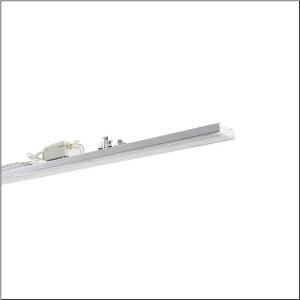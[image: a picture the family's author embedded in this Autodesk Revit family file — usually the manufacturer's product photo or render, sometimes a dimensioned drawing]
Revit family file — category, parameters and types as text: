
# Revit family: licross_r__21_recessed_mo_52te10dv4e5g_8208
name_source: partatom
category: Lighting Fixtures
units: mm (PartAtom-declared; Revit-internal decimal feet)

## family parameters
Cut with Voids When Loaded = No
Host = Face
Light Source = No
Part Type = Normal
Room Calculation Point = No
Round Connector Dimension = Use Diameter
Shared = No

## types (1)
- --- (1 x LED, 14990 lm, 85.3 W, 4000K)
    Apparent Load = 85 VA
    CIE Flux Codes = 50 81 96 100 100
    Color Rendering = 80
    Color Temperature = 4000K
    Default Elevation = 1800 mm
    Description = Licross® 21 Recessed MO, luminaire insert, of sheet steel, galvanised, coil coated, white, length: 2.250mm, width: 66mm, height: 67mm, LED rated luminous flux: 14.990lm, light colour: 840, control gear: DALI 2, with plug, 5-pole, with phase selection, mains connection: 220..240V, AC, 50/60Hz, rated input power: 85W, halogen-free wiring, primary optical cover: cover, of PMMA, light emission: direct distribution, primary light characteristic: symmetric, protection rating (complete): IP54, insulation class (complete): insulation class I (protective earthing), certification: CE, ENEC, VDE, UKCA, protection symbol: D if used in an environment with non-conductive dust loads with corresponding accessories, impact resistance: IK06, permissible ambient temperature for indoor applications: -25..+35°C, corresponds to IFS (International Featured Standards) requirements for safety and quality in the food industry, reducing of maximum allowable ambient temperature of 5°C with ceiling mounting, LABS conformity tested according to VDMA 24364:2018-05, packaging unit: 1 piece
    Height = 58 mm
    Lamp = 1 x LED
    Lamp Light Flux = 14990 lm
    Lamp Power = 85.3 W
    Lamp count = 1
    Length = 2250 mm
    Luminous efficacy = 176 lm/W
    Manufacturer = Siteco
    ModVariant = No
    Model = 52TE10DV4E5G
    Mounting Place = Ceiling
    Mounting Type = Pendant
    Number of Poles = 1
    OnlyDefault = Yes
    Power Factor = 1
    Product Name = Licross® 21 Recessed MO
    Product group = luminaire insert
    ProductGroupID = 901
    Protection Class = Protection class I
    Protection Degree = IP 54
    RLX_Detail_Level = 1
    RLX_Emergency_Light_Flux = 0 lm
    RLX_Emergency_Type = 0
    RLX_Emergency_Type_DB = No
    RlxData = <blob elided: 29341 chars, md5=07ba838a>
    Socket = socket
    Standby Power = 0 W
    System Light Flux = 14990 lm
    System Power = 85 W
    Type Comments = factory setting: luminous flux: 100 % | dim-lin: 254 | 390 mA
    Type Image = l_1296930.jpg
    URL = http://relux.com
    VarID = @adj_059203
    Voltage = 0 V
    Weight = 0.00 kg
    Width = 66 mm

## geometry (parser evidence)
native form markers: Blend x4, Sweep x10
no freeform markers — native parametric forms only
